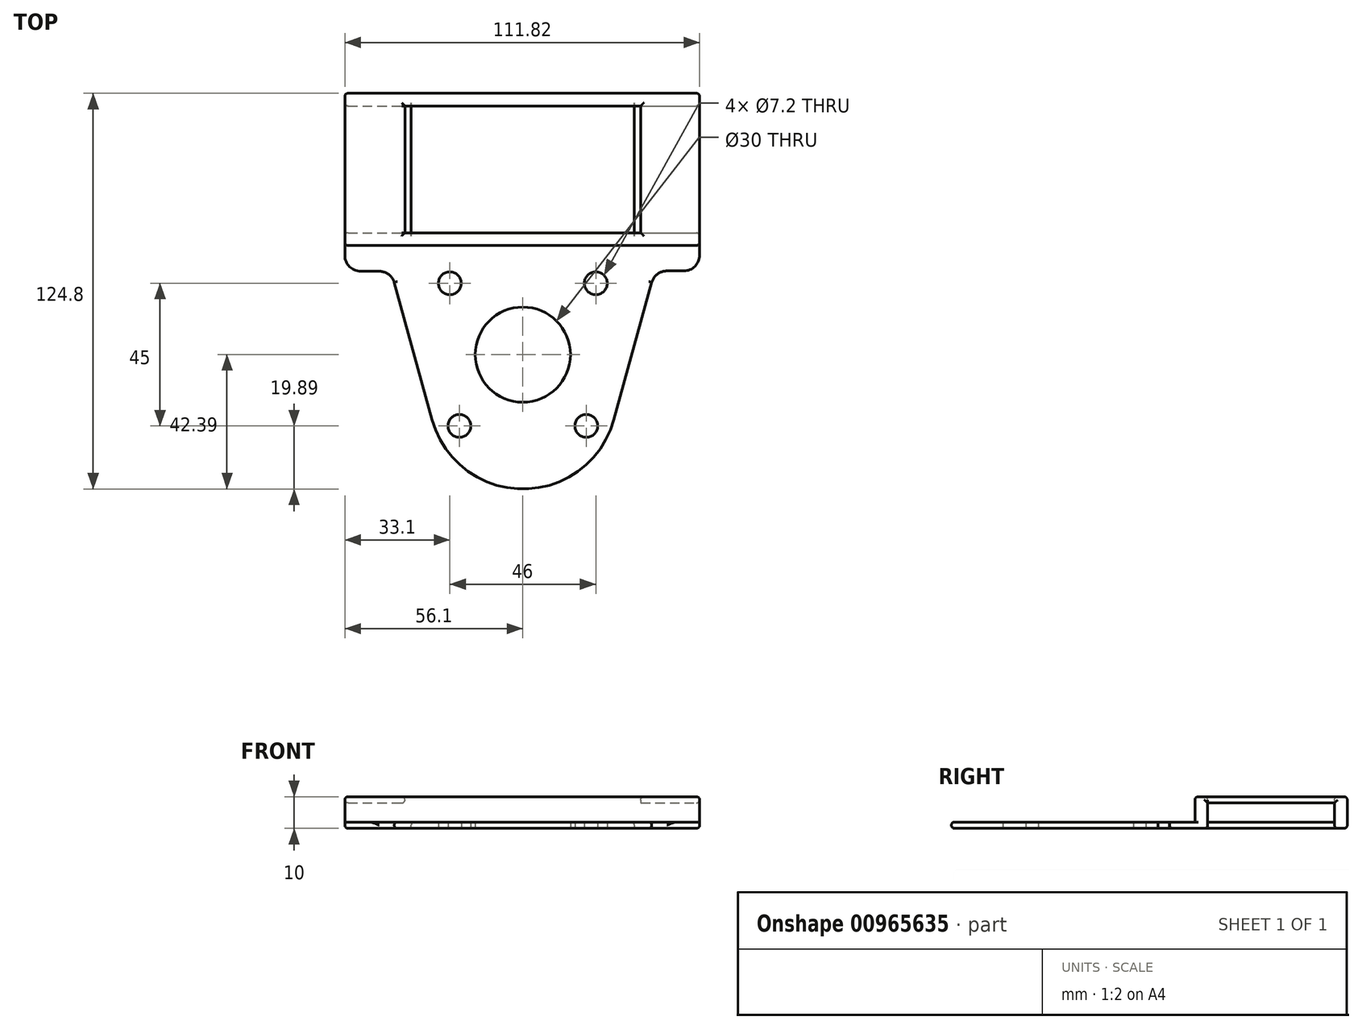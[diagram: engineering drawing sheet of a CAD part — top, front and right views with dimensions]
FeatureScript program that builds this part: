
annotation { "Feature Type Name" : "Feature", "Feature Type Description" : "" }
export const myFeature = defineFeature(function(context is Context, id is Id, definition is map)
    precondition{}
    {
        {
            assignVariable(context, id + "F0", {"name" : "Hole1", "anyValue" : 30});
        }
        {
            assignVariable(context, id + "F1", {"name" : "Hole2", "anyValue" : 7.2});
        }
        {
            var Q0;
            Q0=qCreatedBy(makeId("Top.planeOp"),FACE);
            var sketch = newSketch(context, id + "F2", { "sketchPlane" : qUnion([Q0])});
            skLineSegment(sketch, "E0", {"start": v(0, 0) * mm, "end": v(0, 83.86) * mm, "construction": true});
            skPoint(sketch, "E1.middle", {"position": v(0, 0) * mm});
            skArc(sketch, "E2", {"start": v(-28.58, -20.58) * mm, "mid": v(0.05, -42.39) * mm, "end": v(28.67, -20.58) * mm});
            skLineSegment(sketch, "E3", {"start": v(0, 0) * mm, "end": v(0, -55.96) * mm, "construction": true});
            skLineSegment(sketch, "E4", {"start": v(-29.7, 0) * mm, "end": v(29.7, 0) * mm, "construction": true});
            skLineSegment(sketch, "E5.MirrorCS", {"start": v(-56.1, 82.4) * mm, "end": v(55.72, 82.4) * mm});
            skLineSegment(sketch, "E6", {"start": v(55.72, 82.4) * mm, "end": v(55.72, 31.39) * mm});
            skLineSegment(sketch, "E7", {"start": v(50.72, 26.39) * mm, "end": v(45.42, 26.39) * mm});
            skLineSegment(sketch, "E8", {"start": v(-56.1, 82.4) * mm, "end": v(-56.1, 31.29) * mm});
            skLineSegment(sketch, "E9", {"start": v(-51.1, 26.29) * mm, "end": v(-45.3, 26.29) * mm});
            skArc(sketch, "E10.filletArc", {"start": v(45.42, 26.39) * mm, "mid": v(42.42, 25.38) * mm, "end": v(40.62, 22.77) * mm});
            skArc(sketch, "E11.filletArc", {"start": v(-40.52, 22.77) * mm, "mid": v(-42.33, 25.31) * mm, "end": v(-45.3, 26.29) * mm});
            skLineSegment(sketch, "E12", {"start": v(-56.1, 78.4) * mm, "end": v(55.72, 78.4) * mm});
            skLineSegment(sketch, "E13", {"start": v(28.67, -20.58) * mm, "end": v(40.62, 22.77) * mm});
            skLineSegment(sketch, "E14", {"start": v(-28.58, -20.58) * mm, "end": v(-40.52, 22.77) * mm});
            skArc(sketch, "E15.filletArc", {"start": v(-56.1, 31.29) * mm, "mid": v(-54.63, 27.75) * mm, "end": v(-51.1, 26.29) * mm});
            skArc(sketch, "E16.filletArc", {"start": v(50.72, 26.39) * mm, "mid": v(54.26, 27.85) * mm, "end": v(55.72, 31.39) * mm});
            skLineSegment(sketch, "E17", {"start": v(-56.1, 34.4) * mm, "end": v(55.72, 34.4) * mm});
            skLineSegment(sketch, "E18", {"start": v(-56.1, 38.4) * mm, "end": v(55.72, 38.4) * mm});
            skLineSegment(sketch, "E19", {"start": v(35.18, 78.4) * mm, "end": v(35.18, 38.4) * mm});
            skLineSegment(sketch, "E20", {"start": v(37.18, 78.4) * mm, "end": v(37.18, 38.4) * mm});
            skLineSegment(sketch, "E21.MirrorCS", {"start": v(-35.18, 78.4) * mm, "end": v(-35.18, 38.4) * mm});
            skLineSegment(sketch, "E22.MirrorCS", {"start": v(-37.18, 78.4) * mm, "end": v(-37.18, 38.4) * mm});
            skSolve(sketch);
        }
        {
            var Q0;
            Q0=qCreatedBy(makeId("Top.planeOp"),FACE);
            var sketch = newSketch(context, id + "F3", { "sketchPlane" : qUnion([Q0])});
            skCircle(sketch, "E23", {"center": v(0, 0) * mm, "radius": 15 * mm});
            skLineSegment(sketch, "E24", {"start": v(0, 0) * mm, "end": v(0, 22.5) * mm, "construction": true});
            skLineSegment(sketch, "E25", {"start": v(0, 22.5) * mm, "end": v(23, 22.5) * mm, "construction": true});
            skLineSegment(sketch, "E26", {"start": v(0, 0) * mm, "end": v(0, -22.5) * mm, "construction": true});
            skLineSegment(sketch, "E27", {"start": v(0, -22.5) * mm, "end": v(-20, -22.5) * mm, "construction": true});
            skLineSegment(sketch, "E28.MirrorCS", {"start": v(0, 22.5) * mm, "end": v(-23, 22.5) * mm, "construction": true});
            skLineSegment(sketch, "E29.MirrorCS", {"start": v(0, -22.5) * mm, "end": v(20, -22.5) * mm, "construction": true});
            skCircle(sketch, "E30", {"center": v(-23, 22.5) * mm, "radius": 3.6 * mm});
            skCircle(sketch, "E31", {"center": v(23, 22.5) * mm, "radius": 3.6 * mm});
            skCircle(sketch, "E32", {"center": v(20, -22.5) * mm, "radius": 3.6 * mm});
            skCircle(sketch, "E33", {"center": v(-20, -22.5) * mm, "radius": 3.6 * mm});
            skLineSegment(sketch, "E34", {"start": v(0, -22.5) * mm, "end": v(0, -56.24) * mm, "construction": true});
            skLineSegment(sketch, "E35", {"start": v(-29.7, 0) * mm, "end": v(29.7, 0) * mm, "construction": true});
            skLineSegment(sketch, "E36", {"start": v(0, 22.5) * mm, "end": v(0, 78.62) * mm, "construction": true});
            skSolve(sketch);
        }
        {
            var Q0;
            {var subQ0=sQuery(id+"F2.wireOp",EDGE,"E19");Q0=makeQuery(id+"F2.imprint","IMPRINT",FACE,{"disambiguationData":[TD([[makeQuery(id+"F2.imprint","IMPRINT",EDGE,{"derivedFrom":subQ0}),-1.0]])]});}
            var Q1;
            Q1=makeQuery(id+"F2.imprint","IMPRINT",FACE,{"disambiguationData":[TD([[makeQuery(id+"F2.imprint","IMPRINT",EDGE,{"derivedFrom":sQuery(id+"F2.wireOp",EDGE,"E2")}),1.0]])]});
            extrude(context, id + "F4", {"entities" : qUnion([Q0, Q1]), "depth" : 2 * mm, "offsetDistance" : 25 * mm});
        }
        {
            var Q0;
            {var subQ4=sQuery(id+"F2.wireOp",EDGE,"E5.MirrorCS");Q0=makeQuery(id+"F2.imprint","IMPRINT",FACE,{"disambiguationData":[TD([[makeQuery(id+"F2.imprint","IMPRINT",EDGE,{"derivedFrom":subQ4}),-1.0]])]});}
            var Q1;
            {var subQ4=sQuery(id+"F2.wireOp",EDGE,"E17");Q1=makeQuery(id+"F2.imprint","IMPRINT",FACE,{"disambiguationData":[TD([[makeQuery(id+"F2.imprint","IMPRINT",EDGE,{"derivedFrom":subQ4}),1.0]])]});}
            extrude(context, id + "F5", {"entities" : qUnion([Q0, Q1]), "depth" : 10 * mm, "offsetDistance" : 25 * mm});
        }
        {
            var Q0;
            Q0=sQuery(id+"F3.wireOp",VERTEX,"E28.MirrorCS.end");
            var Q1;
            Q1=sQuery(id+"F3.wireOp",VERTEX,"E25.end");
            var Q2;
            Q2=sQuery(id+"F3.wireOp",VERTEX,"E29.MirrorCS.end");
            var Q3;
            Q3=sQuery(id+"F3.wireOp",VERTEX,"E27.end");
            var Q4;
            Q4=makeQuery(id+"F4.opExtrude","SWEPT_BODY",BODY,{"disambiguationData":[OSD([sQuery(id+"F2.wireOp",EDGE,"E2"),sQuery(id+"F2.wireOp",EDGE,"E6"),sQuery(id+"F2.wireOp",EDGE,"E7"),sQuery(id+"F2.wireOp",EDGE,"E8"),sQuery(id+"F2.wireOp",EDGE,"E9"),sQuery(id+"F2.wireOp",EDGE,"E10.filletArc"),sQuery(id+"F2.wireOp",EDGE,"E11.filletArc"),sQuery(id+"F2.wireOp",EDGE,"E13"),sQuery(id+"F2.wireOp",EDGE,"E14"),sQuery(id+"F2.wireOp",EDGE,"E15.filletArc"),sQuery(id+"F2.wireOp",EDGE,"E16.filletArc"),sQuery(id+"F2.wireOp",EDGE,"E17")])]});
            hole(context, id + "F6", {"style" : HoleStyle.SIMPLE, "endStyle" : HoleEndStyle.THROUGH, "oppositeDirection" : true, "holeDiameter" : (getVariable(context, 'Hole2')) * mm, "majorDiameter" : 5 * mm, "isTappedThrough" : true, "tappedDepth" : 12 * mm, "tapClearance" : 3, "startFromSketch" : true, "locations" : qUnion([Q0, Q1, Q2, Q3]), "scope" : qUnion([Q4])});
        }
        {
            var Q0;
            Q0=sQuery(id+"F2.wireOp",VERTEX,"E1.middle");
            var Q1;
            Q1=makeQuery(id+"F4.opExtrude","SWEPT_BODY",BODY,{"disambiguationData":[OSD([sQuery(id+"F2.wireOp",EDGE,"E2"),sQuery(id+"F2.wireOp",EDGE,"E6"),sQuery(id+"F2.wireOp",EDGE,"E7"),sQuery(id+"F2.wireOp",EDGE,"E8"),sQuery(id+"F2.wireOp",EDGE,"E9"),sQuery(id+"F2.wireOp",EDGE,"E10.filletArc"),sQuery(id+"F2.wireOp",EDGE,"E11.filletArc"),sQuery(id+"F2.wireOp",EDGE,"E13"),sQuery(id+"F2.wireOp",EDGE,"E14"),sQuery(id+"F2.wireOp",EDGE,"E15.filletArc"),sQuery(id+"F2.wireOp",EDGE,"E16.filletArc"),sQuery(id+"F2.wireOp",EDGE,"E17")])]});
            hole(context, id + "F7", {"style" : HoleStyle.SIMPLE, "endStyle" : HoleEndStyle.THROUGH, "oppositeDirection" : true, "holeDiameter" : (getVariable(context, 'Hole1')) * mm, "majorDiameter" : 5 * mm, "isTappedThrough" : true, "tappedDepth" : 12 * mm, "tapClearance" : 3, "startFromSketch" : true, "locations" : qUnion([Q0]), "scope" : qUnion([Q1])});
        }
        {
            var Q0;
            {var subQ5=sQuery(id+"F2.wireOp",EDGE,"E22.MirrorCS");Q0=makeQuery(id+"F2.imprint","IMPRINT",FACE,{"disambiguationData":[TD([[makeQuery(id+"F2.imprint","IMPRINT",EDGE,{"derivedFrom":subQ5}),-1.0]])]});}
            var Q1;
            {var subQ5=sQuery(id+"F2.wireOp",EDGE,"E20");Q1=makeQuery(id+"F2.imprint","IMPRINT",FACE,{"disambiguationData":[TD([[makeQuery(id+"F2.imprint","IMPRINT",EDGE,{"derivedFrom":subQ5}),1.0]])]});}
            extrude(context, id + "F8", {"entities" : qUnion([Q0, Q1]), "surfaceOperationType" : NewSurfaceOperationType.ADD, "depth" : 10 * mm, "offsetDistance" : 25 * mm, "hasSecondDirection" : true, "secondDirectionOppositeDirection" : false, "secondDirectionDepth" : 8 * mm});
        }
        {
            var Q0;
            Q0=makeQuery(id+"F5.opExtrude","SWEPT_BODY",BODY,{"disambiguationData":[OSD([sQuery(id+"F2.wireOp",EDGE,"E6"),sQuery(id+"F2.wireOp",EDGE,"E8"),sQuery(id+"F2.wireOp",EDGE,"E17"),sQuery(id+"F2.wireOp",EDGE,"E18")])]});
            var Q1;
            Q1=makeQuery(id+"F4.opExtrude","SWEPT_BODY",BODY,{"disambiguationData":[OSD([sQuery(id+"F2.wireOp",EDGE,"E2"),sQuery(id+"F2.wireOp",EDGE,"E6"),sQuery(id+"F2.wireOp",EDGE,"E7"),sQuery(id+"F2.wireOp",EDGE,"E8"),sQuery(id+"F2.wireOp",EDGE,"E9"),sQuery(id+"F2.wireOp",EDGE,"E10.filletArc"),sQuery(id+"F2.wireOp",EDGE,"E11.filletArc"),sQuery(id+"F2.wireOp",EDGE,"E13"),sQuery(id+"F2.wireOp",EDGE,"E14"),sQuery(id+"F2.wireOp",EDGE,"E15.filletArc"),sQuery(id+"F2.wireOp",EDGE,"E16.filletArc"),sQuery(id+"F2.wireOp",EDGE,"E17")])]});
            var Q2;
            Q2=makeQuery(id+"F8.opExtrude","SWEPT_BODY",BODY,{"disambiguationData":[OSD([sQuery(id+"F2.wireOp",EDGE,"E8"),sQuery(id+"F2.wireOp",EDGE,"E12"),sQuery(id+"F2.wireOp",EDGE,"E18"),sQuery(id+"F2.wireOp",EDGE,"E22.MirrorCS")])]});
            var Q3;
            Q3=makeQuery(id+"F5.opExtrude","SWEPT_BODY",BODY,{"disambiguationData":[OSD([sQuery(id+"F2.wireOp",EDGE,"E5.MirrorCS"),sQuery(id+"F2.wireOp",EDGE,"E6"),sQuery(id+"F2.wireOp",EDGE,"E8"),sQuery(id+"F2.wireOp",EDGE,"E12")])]});
            var Q4;
            Q4=makeQuery(id+"F4.opExtrude","SWEPT_BODY",BODY,{"disambiguationData":[OSD([sQuery(id+"F2.wireOp",EDGE,"E12"),sQuery(id+"F2.wireOp",EDGE,"E18"),sQuery(id+"F2.wireOp",EDGE,"E19"),sQuery(id+"F2.wireOp",EDGE,"E21.MirrorCS")])]});
            var Q5;
            Q5=makeQuery(id+"F8.opExtrude","SWEPT_BODY",BODY,{"disambiguationData":[OSD([sQuery(id+"F2.wireOp",EDGE,"E6"),sQuery(id+"F2.wireOp",EDGE,"E12"),sQuery(id+"F2.wireOp",EDGE,"E18"),sQuery(id+"F2.wireOp",EDGE,"E20")])]});
            booleanBodies(context, id + "F9", {"operationType" : BooleanOperationType.UNION, "tools" : qUnion([Q0, Q1, Q2, Q3, Q4, Q5])});
        }
        {
            var Q0;
            Q0=makeQuery(id+"F5.opExtrude","CAP_EDGE",EDGE,{"disambiguationData":[OSD([sQuery(id+"F2.wireOp",EDGE,"E5.MirrorCS")])],"isStart":true});
            var Q1;
            Q1=makeQuery(id+"F5.opExtrude","CAP_EDGE",EDGE,{"disambiguationData":[OSD([sQuery(id+"F2.wireOp",EDGE,"E5.MirrorCS")])],"isStart":false});
            var Q2;
            Q2=makeQuery(id+"F5.opExtrude","SWEPT_EDGE",EDGE,{"disambiguationData":[OSD([sQuery(id+"F2.wireOp",EDGE,"E5.MirrorCS"),sQuery(id+"F2.wireOp",EDGE,"E6")])]});
            var Q3;
            Q3=makeQuery(id+"F5.opExtrude","SWEPT_EDGE",EDGE,{"disambiguationData":[OSD([sQuery(id+"F2.wireOp",EDGE,"E5.MirrorCS"),sQuery(id+"F2.wireOp",EDGE,"E8")])]});
            var Q4;
            {var subQ0=sQuery(id+"F2.wireOp",EDGE,"E8");Q4=makeQuery(id+"F9.opBoolean","MERGE",EDGE,{"derivedFrom":[makeQuery(id+"F5.opExtrude","CAP_EDGE",EDGE,{"disambiguationData":[OSD([subQ0]),TDD([makeQuery(id+"F2.imprint","IMPRINT",EDGE,{"disambiguationData":[TD([[makeQuery(id+"F2.imprint","INTERSECT",VERTEX,{"derivedFrom":[sQuery(id+"F2.wireOp",EDGE,"E5.MirrorCS"),subQ0]}),-1.0]])],"derivedFrom":subQ0})])],"isStart":false}),makeQuery(id+"F5.opExtrude","CAP_EDGE",EDGE,{"disambiguationData":[OSD([subQ0]),TDD([makeQuery(id+"F2.imprint","IMPRINT",EDGE,{"disambiguationData":[TD([[makeQuery(id+"F2.imprint","INTERSECT",VERTEX,{"derivedFrom":[subQ0,sQuery(id+"F2.wireOp",EDGE,"E17")]}),1.0]])],"derivedFrom":subQ0})])],"isStart":false}),makeQuery(id+"F8.opExtrude","CAP_EDGE",EDGE,{"disambiguationData":[OSD([subQ0])],"isStart":false})]});}
            var Q5;
            {var subQ0=sQuery(id+"F2.wireOp",EDGE,"E6");Q5=makeQuery(id+"F9.opBoolean","MERGE",EDGE,{"derivedFrom":[makeQuery(id+"F5.opExtrude","CAP_EDGE",EDGE,{"disambiguationData":[OSD([subQ0]),TDD([makeQuery(id+"F2.imprint","IMPRINT",EDGE,{"disambiguationData":[TD([[makeQuery(id+"F2.imprint","INTERSECT",VERTEX,{"derivedFrom":[sQuery(id+"F2.wireOp",EDGE,"E5.MirrorCS"),subQ0]}),-1.0]])],"derivedFrom":subQ0})])],"isStart":false}),makeQuery(id+"F5.opExtrude","CAP_EDGE",EDGE,{"disambiguationData":[OSD([subQ0]),TDD([makeQuery(id+"F2.imprint","IMPRINT",EDGE,{"disambiguationData":[TD([[makeQuery(id+"F2.imprint","INTERSECT",VERTEX,{"derivedFrom":[subQ0,sQuery(id+"F2.wireOp",EDGE,"E17")]}),1.0]])],"derivedFrom":subQ0})])],"isStart":false}),makeQuery(id+"F8.opExtrude","CAP_EDGE",EDGE,{"disambiguationData":[OSD([subQ0])],"isStart":false})]});}
            var Q6;
            Q6=makeQuery(id+"F5.opExtrude","CAP_EDGE",EDGE,{"disambiguationData":[OSD([sQuery(id+"F2.wireOp",EDGE,"E12")])],"isStart":false});
            var Q7;
            Q7=makeQuery(id+"F8.opExtrude","CAP_EDGE",EDGE,{"disambiguationData":[OSD([sQuery(id+"F2.wireOp",EDGE,"E22.MirrorCS")])],"isStart":false});
            var Q8;
            Q8=makeQuery(id+"F8.opExtrude","CAP_EDGE",EDGE,{"disambiguationData":[OSD([sQuery(id+"F2.wireOp",EDGE,"E8")])],"isStart":true});
            var Q9;
            Q9=makeQuery(id+"F5.opExtrude","CAP_EDGE",EDGE,{"disambiguationData":[OSD([sQuery(id+"F2.wireOp",EDGE,"E17")])],"isStart":false});
            var Q10;
            Q10=makeQuery(id+"F8.opExtrude","CAP_EDGE",EDGE,{"disambiguationData":[OSD([sQuery(id+"F2.wireOp",EDGE,"E22.MirrorCS")])],"isStart":true});
            var Q11;
            Q11=makeQuery(id+"F5.opExtrude","CAP_EDGE",EDGE,{"disambiguationData":[OSD([sQuery(id+"F2.wireOp",EDGE,"E18")])],"isStart":false});
            var Q12;
            Q12=makeQuery(id+"F8.opExtrude","CAP_EDGE",EDGE,{"disambiguationData":[OSD([sQuery(id+"F2.wireOp",EDGE,"E20")])],"isStart":false});
            var Q13;
            {var subQ0=sQuery(id+"F2.wireOp",EDGE,"E6");Q13=makeQuery(id+"F5.opExtrude","CAP_EDGE",EDGE,{"disambiguationData":[OSD([subQ0]),TDD([makeQuery(id+"F2.imprint","IMPRINT",EDGE,{"disambiguationData":[TD([[makeQuery(id+"F2.imprint","INTERSECT",VERTEX,{"derivedFrom":[sQuery(id+"F2.wireOp",EDGE,"E5.MirrorCS"),subQ0]}),-1.0]])],"derivedFrom":subQ0})])],"isStart":true});}
            var Q14;
            Q14=makeQuery(id+"F5.opExtrude","SWEPT_EDGE",EDGE,{"disambiguationData":[OSD([sQuery(id+"F2.wireOp",EDGE,"E6"),sQuery(id+"F2.wireOp",EDGE,"E12")])]});
            var Q15;
            Q15=makeQuery(id+"F8.opExtrude","CAP_EDGE",EDGE,{"disambiguationData":[OSD([sQuery(id+"F2.wireOp",EDGE,"E6")])],"isStart":true});
            var Q16;
            Q16=makeQuery(id+"F5.opExtrude","SWEPT_EDGE",EDGE,{"disambiguationData":[OSD([sQuery(id+"F2.wireOp",EDGE,"E6"),sQuery(id+"F2.wireOp",EDGE,"E18")])]});
            var Q17;
            Q17=makeQuery(id+"F5.opExtrude","SWEPT_EDGE",EDGE,{"disambiguationData":[OSD([sQuery(id+"F2.wireOp",EDGE,"E6"),sQuery(id+"F2.wireOp",EDGE,"E17")])]});
            var Q18;
            Q18=makeQuery(id+"F5.opExtrude","SWEPT_EDGE",EDGE,{"disambiguationData":[OSD([sQuery(id+"F2.wireOp",EDGE,"E8"),sQuery(id+"F2.wireOp",EDGE,"E17")])]});
            var Q19;
            Q19=makeQuery(id+"F5.opExtrude","SWEPT_EDGE",EDGE,{"disambiguationData":[OSD([sQuery(id+"F2.wireOp",EDGE,"E8"),sQuery(id+"F2.wireOp",EDGE,"E18")])]});
            var Q20;
            Q20=makeQuery(id+"F5.opExtrude","SWEPT_EDGE",EDGE,{"disambiguationData":[OSD([sQuery(id+"F2.wireOp",EDGE,"E8"),sQuery(id+"F2.wireOp",EDGE,"E12")])]});
            var Q21;
            {var subQ0=sQuery(id+"F2.wireOp",EDGE,"E8");Q21=makeQuery(id+"F5.opExtrude","CAP_EDGE",EDGE,{"disambiguationData":[OSD([subQ0]),TDD([makeQuery(id+"F2.imprint","IMPRINT",EDGE,{"disambiguationData":[TD([[makeQuery(id+"F2.imprint","INTERSECT",VERTEX,{"derivedFrom":[sQuery(id+"F2.wireOp",EDGE,"E5.MirrorCS"),subQ0]}),-1.0]])],"derivedFrom":subQ0})])],"isStart":true});}
            var Q22;
            {var subQ2=sQuery(id+"F2.wireOp",EDGE,"E12");var subQ3=sQuery(id+"F2.wireOp",EDGE,"E6");Q22=makeQuery(id+"F9.opBoolean","SPLIT",EDGE,{"disambiguationData":[TD([makeQuery(id+"F4.opExtrude","SWEPT_FACE",FACE,{"disambiguationData":[OSD([subQ3])]})])],"derivedFrom":makeQuery(id+"F5.opExtrude","CAP_EDGE",EDGE,{"disambiguationData":[OSD([subQ2])],"isStart":true})});}
            var Q23;
            {var subQ2=sQuery(id+"F2.wireOp",EDGE,"E12");var subQ3=sQuery(id+"F2.wireOp",EDGE,"E8");Q23=makeQuery(id+"F9.opBoolean","SPLIT",EDGE,{"disambiguationData":[TD([makeQuery(id+"F4.opExtrude","SWEPT_FACE",FACE,{"disambiguationData":[OSD([subQ3])]})])],"derivedFrom":makeQuery(id+"F5.opExtrude","CAP_EDGE",EDGE,{"disambiguationData":[OSD([subQ2])],"isStart":true})});}
            var Q24;
            Q24=makeQuery(id+"F4.opExtrude","CAP_EDGE",EDGE,{"disambiguationData":[OSD([sQuery(id+"F2.wireOp",EDGE,"E12")])],"isStart":false});
            var Q25;
            Q25=makeQuery(id+"F4.opExtrude","CAP_EDGE",EDGE,{"disambiguationData":[OSD([sQuery(id+"F2.wireOp",EDGE,"E21.MirrorCS")])],"isStart":false});
            var Q26;
            Q26=makeQuery(id+"F4.opExtrude","CAP_EDGE",EDGE,{"disambiguationData":[OSD([sQuery(id+"F2.wireOp",EDGE,"E19")])],"isStart":false});
            var Q27;
            Q27=makeQuery(id+"F4.opExtrude","CAP_EDGE",EDGE,{"disambiguationData":[OSD([sQuery(id+"F2.wireOp",EDGE,"E18")])],"isStart":false});
            var Q28;
            Q28=makeQuery(id+"F4.opExtrude","CAP_EDGE",EDGE,{"disambiguationData":[OSD([sQuery(id+"F2.wireOp",EDGE,"E17")])],"isStart":false});
            var Q29;
            Q29=makeQuery(id+"F4.opExtrude","CAP_EDGE",EDGE,{"disambiguationData":[OSD([sQuery(id+"F2.wireOp",EDGE,"E13")])],"isStart":false});
            fillet(context, id + "F10", {"entities" : qUnion([Q0, Q1, Q2, Q3, Q4, Q5, Q6, Q7, Q8, Q9, Q10, Q11, Q12, Q13, Q14, Q15, Q16, Q17, Q18, Q19, Q20, Q21, Q22, Q23, Q24, Q25, Q26, Q27, Q28, Q29]), "radius" : 1 * mm, "tangentPropagation" : true, "allowEdgeOverflow" : false});
        }
        {
            var Q0;
            {var subQ0=sQuery(id+"F2.wireOp",EDGE,"E8");Q0=makeQuery(id+"F9.opBoolean","MERGE",EDGE,{"derivedFrom":[makeQuery(id+"F4.opExtrude","CAP_EDGE",EDGE,{"disambiguationData":[OSD([subQ0])],"isStart":true}),makeQuery(id+"F5.opExtrude","CAP_EDGE",EDGE,{"disambiguationData":[OSD([subQ0]),TDD([makeQuery(id+"F2.imprint","IMPRINT",EDGE,{"disambiguationData":[TD([[makeQuery(id+"F2.imprint","INTERSECT",VERTEX,{"derivedFrom":[subQ0,sQuery(id+"F2.wireOp",EDGE,"E17")]}),1.0]])],"derivedFrom":subQ0})])],"isStart":true})]});}
            var Q1;
            Q1=makeQuery(id+"F4.opExtrude","CAP_EDGE",EDGE,{"disambiguationData":[OSD([sQuery(id+"F2.wireOp",EDGE,"E14")])],"isStart":true});
            var Q2;
            {var subQ0=sQuery(id+"F2.wireOp",EDGE,"E6");Q2=makeQuery(id+"F9.opBoolean","MERGE",EDGE,{"derivedFrom":[makeQuery(id+"F4.opExtrude","CAP_EDGE",EDGE,{"disambiguationData":[OSD([subQ0])],"isStart":true}),makeQuery(id+"F5.opExtrude","CAP_EDGE",EDGE,{"disambiguationData":[OSD([subQ0]),TDD([makeQuery(id+"F2.imprint","IMPRINT",EDGE,{"disambiguationData":[TD([[makeQuery(id+"F2.imprint","INTERSECT",VERTEX,{"derivedFrom":[subQ0,sQuery(id+"F2.wireOp",EDGE,"E17")]}),1.0]])],"derivedFrom":subQ0})])],"isStart":true})]});}
            fillet(context, id + "F11", {"entities" : qUnion([Q0, Q1, Q2]), "radius" : 1 * mm, "tangentPropagation" : true, "allowEdgeOverflow" : false});
        }
    });
